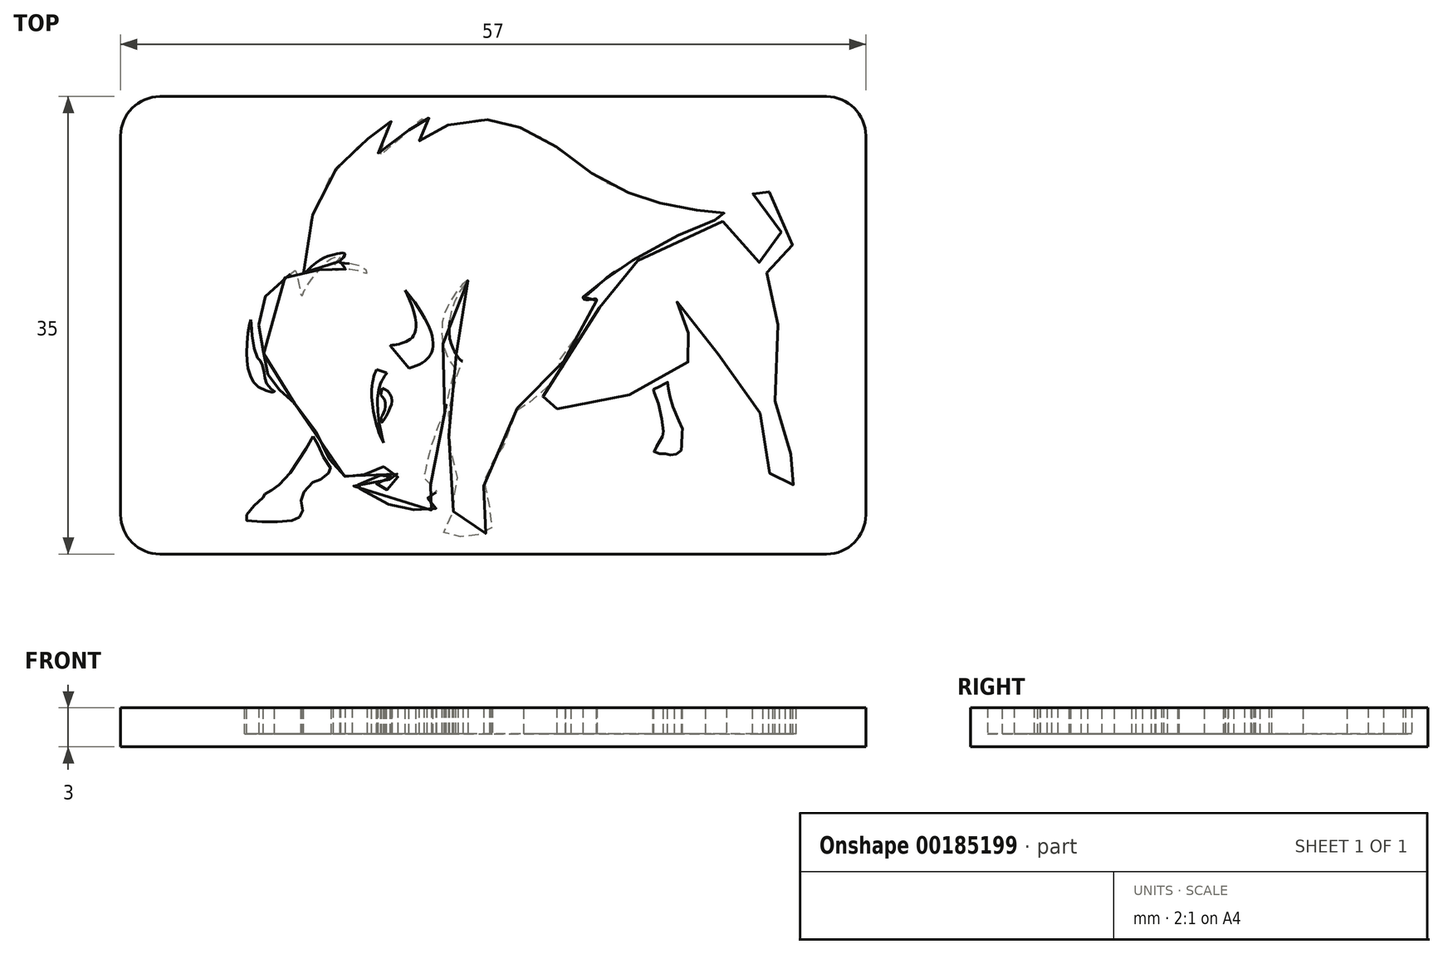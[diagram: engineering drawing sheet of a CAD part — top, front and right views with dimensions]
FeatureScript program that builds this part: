
annotation { "Feature Type Name" : "Feature", "Feature Type Description" : "" }
export const myFeature = defineFeature(function(context is Context, id is Id, definition is map)
    precondition{}
    {
        {
            var Q0;
            Q0=qCreatedBy(makeId("Top.planeOp"),FACE);
            var sketch = newSketch(context, id + "F0", { "sketchPlane" : qUnion([Q0])});
            skLineSegment(sketch, "E0.bottom", {"start": v(25.5, 17.5) * mm, "end": v(-25.5, 17.5) * mm});
            skLineSegment(sketch, "E0.top", {"start": v(25.5, -17.5) * mm, "end": v(-25.5, -17.5) * mm});
            skLineSegment(sketch, "E0.left", {"start": v(28.5, 14.5) * mm, "end": v(28.5, -14.5) * mm});
            skLineSegment(sketch, "E0.right", {"start": v(-28.5, 14.5) * mm, "end": v(-28.5, -14.5) * mm});
            skPoint(sketch, "E0.middle", {"position": v(0, 0) * mm});
            skPoint(sketch, "E1.visualSharp", {"position": v(-28.5, 17.5) * mm});
            skArc(sketch, "E1.filletArc", {"start": v(-25.5, 17.5) * mm, "mid": v(-27.62, 16.62) * mm, "end": v(-28.5, 14.5) * mm});
            skPoint(sketch, "E2.visualSharp", {"position": v(28.5, 17.5) * mm});
            skArc(sketch, "E2.filletArc", {"start": v(28.5, 14.5) * mm, "mid": v(27.62, 16.62) * mm, "end": v(25.5, 17.5) * mm});
            skPoint(sketch, "E3.visualSharp", {"position": v(28.5, -17.5) * mm});
            skArc(sketch, "E3.filletArc", {"start": v(25.5, -17.5) * mm, "mid": v(27.62, -16.62) * mm, "end": v(28.5, -14.5) * mm});
            skPoint(sketch, "E4.visualSharp", {"position": v(-28.5, -17.5) * mm});
            skArc(sketch, "E4.filletArc", {"start": v(-28.5, -14.5) * mm, "mid": v(-27.62, -16.62) * mm, "end": v(-25.5, -17.5) * mm});
            skSolve(sketch);
        }
        {
            var Q0;
            Q0=makeQuery(id+"F0.imprint","IMPRINT",FACE,{"disambiguationData":[TD([[makeQuery(id+"F0.imprint","IMPRINT",EDGE,{"derivedFrom":sQuery(id+"F0.wireOp",EDGE,"E0.bottom")}),1.0]])]});
            extrude(context, id + "F1", {"entities" : qUnion([Q0]), "depth" : 3 * mm});
        }
        {
            var Q0;
            {var subQ0=sQuery(id+"F0.wireOp",EDGE,"E4.filletArc");var subQ1=sQuery(id+"F0.wireOp",EDGE,"E3.filletArc");var subQ2=sQuery(id+"F0.wireOp",EDGE,"E2.filletArc");var subQ3=sQuery(id+"F0.wireOp",EDGE,"E1.filletArc");var subQ4=sQuery(id+"F0.wireOp",EDGE,"E0.bottom");var subQ5=sQuery(id+"F0.wireOp",EDGE,"E0.top");var subQ6=sQuery(id+"F0.wireOp",EDGE,"E0.left");var subQ7=sQuery(id+"F0.wireOp",EDGE,"E0.right");Q0=makeQuery(id+"FHE5nEUfE7JCKJp_1.boolean.opBoolean","SPLIT",FACE,{"disambiguationData":[TD([makeQuery(id+"F1.opExtrude","SWEPT_FACE",FACE,{"disambiguationData":[OSD([subQ4])]})])],"derivedFrom":makeQuery(id+"F1.opExtrude","CAP_FACE",FACE,{"disambiguationData":[OSD([subQ4,subQ5,subQ6,subQ7,subQ3,subQ2,subQ1,subQ0])],"isStart":false})});}
            var sketch = newSketch(context, id + "F2", { "sketchPlane" : qUnion([Q0])});
            skFitSpline(sketch, "E5", {"points": [v(-14.5, 4.03) * mm, v(-13.34, 9.77) * mm, v(-10.97, 13.1) * mm, v(-8.71, 14.94) * mm, v(-7.8, 15.6) * mm, v(-7.94, 15.33) * mm, v(-8.84, 12.97) * mm, v(-8.73, 12.95) * mm, v(-4.8, 16.27) * mm, v(-4.75, 16.19) * mm, v(-5.21, 15.38) * mm, v(-5.7, 14.14) * mm, v(-5.57, 14.13) * mm, v(-3.95, 15.13) * mm, v(-0.99, 15.77) * mm, v(0.92, 15.5) * mm, v(3.22, 14.63) * mm, v(6.02, 12.8) * mm, v(8.6, 10.95) * mm, v(11.2, 9.84) * mm, v(12.85, 9.32) * mm, v(15.26, 8.84) * mm, v(17.1, 8.63) * mm, v(17.75, 8.57) * mm, v(17.84, 8.52) * mm, v(17.57, 8.29) * mm, v(16.7, 7.96) * mm, v(13.8, 6.71) * mm, v(10, 4.57) * mm, v(8.54, 3.53) * mm, v(7.15, 2.34) * mm, v(6.86, 2.15) * mm, v(7, 1.99) * mm, v(7.85, 2.02) * mm, v(7.91, 1.9) * mm], "startDerivative": vector(4.07, 101.98) * mm, "endDerivative": vector(-11.12, -29.2) * mm});
            skFitSpline(sketch, "E6", {"points": [v(7.91, 1.9) * mm, v(7.4, 0.74) * mm, v(6.45, -0.72) * mm, v(5.28, -2.23) * mm, v(4.87, -2.58) * mm, v(4.96, -2.86) * mm, v(5.49, -2.73) * mm, v(5.53, -2.84) * mm, v(5.07, -3.53) * mm, v(4.15, -4.71) * mm, v(3.37, -5.44) * mm, v(2.36, -6.12) * mm, v(1.87, -6.3) * mm, v(1.82, -6.4) * mm, v(0.78, -9.2) * mm, v(0.72, -9.36) * mm, v(0.36, -9.87) * mm, v(-0.4, -11) * mm, v(-0.7, -11.93) * mm, v(-0.64, -12.94) * mm, v(-0.25, -13.77) * mm, v(-0.2, -13.92) * mm, v(-0.3, -14.08) * mm, v(-0.28, -14.2) * mm, v(-0.14, -14.67) * mm, v(-0.07, -15.15) * mm, v(-0.14, -15.55) * mm, v(-0.44, -15.86) * mm, v(-1.06, -16.02) * mm, v(-1.88, -16.11) * mm, v(-2.07, -16.16) * mm, v(-3.65, -16.17) * mm, v(-3.73, -16.12) * mm, v(-3.76, -15.74) * mm, v(-3.08, -14.32) * mm, v(-3.06, -14.23) * mm, v(-3.1, -14.12) * mm, v(-3.12, -13.53) * mm, v(-2.73, -12.2) * mm, v(-2.7, -12.02) * mm, v(-2.73, -11.59) * mm, v(-3.1, -10.3) * mm, v(-3.44, -7.36) * mm, v(-3, -4.6) * mm, v(-2.43, -2.98) * mm, v(-2.31, -2.88) * mm, v(-2.37, -2.73) * mm, v(-2.5, -2.67) * mm, v(-2.58, -2.59) * mm, v(-2.97, -1.96) * mm, v(-3.32, -1.02) * mm, v(-3.3, 0.44) * mm, v(-2.89, 1.9) * mm, v(-2.23, 3.01) * mm, v(-1.96, 3.38) * mm, v(-1.96, 3.45) * mm, v(-2.03, 3.45) * mm, v(-2.08, 3.38) * mm, v(-2.2, 3.27) * mm, v(-2.73, 2.68) * mm, v(-3.5, 1.42) * mm, v(-3.87, 0.35) * mm, v(-3.87, -1.18) * mm, v(-3.3, -2.8) * mm, v(-2.9, -3.27) * mm, v(-2.89, -3.34) * mm, v(-2.96, -3.54) * mm, v(-3.1, -3.92) * mm, v(-3.64, -6.5) * mm, v(-3.63, -6.64) * mm, v(-3.69, -6.66) * mm, v(-3.85, -6.93) * mm, v(-4.05, -7.32) * mm, v(-4.9, -9.8) * mm, v(-5.23, -11.26) * mm, v(-5.3, -11.58) * mm, v(-5.3, -11.64) * mm, v(-5.2, -11.76) * mm, v(-4.36, -12.7) * mm, v(-4.36, -12.76) * mm, v(-4.44, -12.8) * mm, v(-5.02, -12.84) * mm, v(-5.09, -12.9) * mm, v(-5.07, -13.02) * mm, v(-4.96, -13.34) * mm, v(-4.73, -13.67) * mm, v(-4.44, -13.94) * mm, v(-4.37, -13.96) * mm, v(-4.4, -14.02) * mm, v(-4.46, -14.05) * mm, v(-4.99, -14.16) * mm, v(-6.43, -14.07) * mm, v(-7.08, -14.01) * mm, v(-8.66, -13.37) * mm, v(-9.93, -12.63) * mm, v(-10.72, -12.26) * mm, v(-10.79, -12.17) * mm, v(-10.69, -12.18) * mm, v(-10.3, -12.19) * mm, v(-9.5, -11.94) * mm, v(-8.64, -11.46) * mm, v(-8.3, -11.32) * mm, v(-7.96, -11.32) * mm, v(-7.76, -11.52) * mm, v(-7.81, -11.7) * mm, v(-8.24, -11.9) * mm, v(-8.9, -12.05) * mm, v(-8.92, -12.13) * mm, v(-8.9, -12.22) * mm, v(-8.4, -12.57) * mm, v(-8.29, -12.62) * mm, v(-8.18, -12.6) * mm, v(-7.5, -12.3) * mm, v(-7.33, -12.1) * mm, v(-7.31, -11.54) * mm, v(-7.55, -11.08) * mm, v(-8.1, -10.82) * mm, v(-8.76, -10.9) * mm, v(-9.44, -11.2) * mm, v(-9.86, -11.44) * mm, v(-10.14, -11.54) * mm, v(-11.24, -11.62) * mm, v(-11.38, -11.53) * mm, v(-11.52, -11.44) * mm, v(-12.28, -10.63) * mm, v(-13.1, -9.06) * mm, v(-13.65, -8) * mm, v(-14.76, -6.58) * mm, v(-15.73, -5.18) * mm, v(-15.84, -5.1) * mm, v(-16.37, -4.9) * mm, v(-16.8, -4.55) * mm, v(-17.1, -4.19) * mm, v(-17.3, -3.27) * mm, v(-17.44, -2.65) * mm, v(-17.71, -1.46) * mm, v(-17.89, -0.55) * mm, v(-17.92, 0.78) * mm, v(-17.5, 2.1) * mm, v(-16.75, 3.05) * mm, v(-15.22, 4.15) * mm, v(-15.12, 4.2) * mm, v(-15.07, 4.1) * mm, v(-15.04, 3.94) * mm, v(-14.7, 2.3) * mm, v(-14.67, 2.23) * mm, v(-14.63, 2.25) * mm, v(-14.6, 2.38) * mm, v(-13.69, 3.8) * mm, v(-12.7, 4.92) * mm, v(-12.38, 5.13) * mm, v(-11.7, 5.32) * mm, v(-11.68, 5.28) * mm, v(-11.93, 4.96) * mm, v(-12.25, 4.32) * mm, v(-12.16, 4.17) * mm, v(-11.9, 4.26) * mm, v(-11.17, 4.3) * mm, v(-10.5, 4.25) * mm, v(-9.8, 4) * mm, v(-9.73, 3.94) * mm, v(-9.66, 4) * mm, v(-9.64, 4.1) * mm, v(-9.72, 4.24) * mm, v(-10.6, 4.67) * mm, v(-11.71, 4.8) * mm, v(-11.75, 4.85) * mm, v(-11.65, 4.98) * mm, v(-11.35, 5.34) * mm, v(-11.35, 5.48) * mm, v(-11.47, 5.53) * mm, v(-11.77, 5.5) * mm, v(-12.4, 5.36) * mm, v(-13.34, 4.94) * mm, v(-14.42, 4.02) * mm, v(-14.5, 3.99) * mm, v(-14.5, 4.03) * mm], "startDerivative": vector(-53.32, -133) * mm, "endDerivative": vector(-2.75, 33.74) * mm});
            skLineSegment(sketch, "E7", {"start": v(-8.92, -3.37) * mm, "end": v(-8.15, -3.64) * mm});
            skFitSpline(sketch, "E8", {"points": [v(-8.15, -3.64) * mm, v(-8.16, -3.7) * mm, v(-8.23, -3.78) * mm, v(-8.53, -4.26) * mm, v(-8.77, -4.95) * mm, v(-8.86, -5.67) * mm, v(-8.83, -6.53) * mm, v(-8.7, -7.64) * mm, v(-8.38, -9) * mm], "startDerivative": vector(0.8, -1.62) * mm, "endDerivative": vector(1.86, -7.3) * mm});
            skFitSpline(sketch, "E9", {"points": [v(-8.38, -9) * mm, v(-8.78, -8.12) * mm, v(-9.14, -6.74) * mm, v(-9.3, -5.37) * mm, v(-9.18, -4.1) * mm, v(-8.92, -3.37) * mm], "startDerivative": vector(-2.22, 4.49) * mm, "endDerivative": vector(1.72, 4.1) * mm});
            skFitSpline(sketch, "E10", {"points": [v(-8.48, -4.8) * mm, v(-8.28, -4.9) * mm, v(-8.03, -5.08) * mm, v(-7.81, -5.38) * mm, v(-7.76, -5.76) * mm, v(-7.8, -6.09) * mm, v(-8.01, -6.6) * mm, v(-8.3, -7.13) * mm, v(-8.5, -7.4) * mm, v(-8.53, -7.4) * mm, v(-8.54, -7.35) * mm, v(-8.57, -7.04) * mm, v(-8.54, -7) * mm, v(-8.4, -6.76) * mm, v(-8.32, -6.56) * mm, v(-8.25, -6.23) * mm, v(-8.27, -5.83) * mm, v(-8.39, -5.57) * mm, v(-8.6, -5.33) * mm, v(-8.6, -5.3) * mm, v(-8.5, -4.83) * mm, v(-8.48, -4.8) * mm]});
            skLineSegment(sketch, "E11", {"start": v(-7.84, -1.61) * mm, "end": v(-6.43, -3.29) * mm});
            skFitSpline(sketch, "E12", {"points": [v(-7.84, -1.61) * mm, v(-7.84, -1.53) * mm, v(-6.85, -1.31) * mm, v(-6.72, 2.67) * mm], "startDerivative": vector(-0.95, 3.07) * mm, "endDerivative": vector(-7.1, 15.2) * mm});
            skFitSpline(sketch, "E13", {"points": [v(-6.72, 2.67) * mm, v(-6.43, -3.29) * mm], "startDerivative": vector(9.14, -11.11) * mm, "endDerivative": vector(-6.63, -1.76) * mm});
            skFitSpline(sketch, "E14", {"points": [v(17.56, 7.97) * mm, v(14.5, 6.71) * mm, v(11.65, 5.26) * mm, v(10.45, 4.56) * mm, v(10.35, 4.45) * mm, v(9.52, 3.5) * mm, v(8.5, 1.92) * mm, v(7.34, 0.1) * mm, v(6.15, -1.64) * mm, v(5.54, -2.39) * mm, v(5.54, -2.4) * mm, v(5.7, -2.4) * mm, v(5.88, -2.44) * mm, v(5.96, -2.54) * mm, v(5.96, -2.69) * mm, v(5.81, -2.96) * mm, v(4.9, -4.28) * mm, v(3.6, -5.62) * mm, v(2.4, -6.41) * mm, v(2.36, -6.43) * mm, v(2.36, -6.47) * mm, v(2.42, -6.48) * mm, v(3.06, -6.43) * mm, v(5.39, -6.36) * mm, v(7.54, -6.1) * mm, v(8.86, -5.8) * mm, v(10.85, -5.16) * mm, v(12.66, -4.4) * mm, v(13.44, -3.85) * mm, v(14.72, -2.92) * mm, v(16.21, -2.07) * mm, v(16.26, -2.04) * mm, v(16.21, -1.97) * mm, v(15.87, -1.71) * mm, v(15.48, -1.28) * mm, v(14.94, -0.63) * mm, v(14.42, 0.34) * mm, v(13.99, 1.54) * mm, v(13.9, 2.2) * mm, v(13.9, 2.22) * mm, v(13.96, 2.22) * mm, v(13.98, 2.15) * mm, v(14.3, 1.12) * mm, v(15.4, -0.49) * mm, v(16.67, -1.85) * mm, v(17.35, -2.29) * mm, v(18.68, -3.64) * mm, v(19.48, -4.85) * mm, v(20.6, -7.13) * mm, v(21.23, -9.34) * mm, v(21.4, -10.55) * mm, v(21.37, -10.64) * mm, v(21.17, -11.24) * mm, v(21.1, -11.96) * mm, v(21.1, -11.99) * mm, v(21.29, -12.12) * mm, v(21.94, -12.33) * mm, v(22.1, -12.34) * mm, v(22.34, -12.32) * mm, v(22.79, -12.26) * mm, v(23.14, -12.11) * mm, v(23.17, -12.08) * mm, v(23.17, -11.9) * mm, v(23.1, -11.62) * mm, v(22.95, -11.18) * mm, v(22.76, -10.84) * mm, v(22.73, -10.81) * mm, v(22.77, -9.89) * mm, v(22.77, -9.85) * mm, v(22.37, -9.03) * mm, v(21.89, -7.8) * mm, v(21.61, -6.73) * mm, v(21.6, -5.27) * mm, v(21.87, -2.84) * mm, v(21.86, -1.13) * mm, v(21.62, 1.1) * mm, v(20.96, 3.19) * mm, v(20.66, 3.83) * mm, v(20.68, 3.97) * mm, v(20.79, 4.04) * mm, v(21.02, 4.02) * mm, v(21.82, 4.06) * mm, v(21.9, 4.07) * mm, v(22.41, 4.28) * mm, v(22.82, 4.8) * mm, v(22.9, 6.03) * mm, v(22.34, 7.64) * mm, v(21.44, 9.32) * mm, v(21.4, 9.44) * mm, v(21.4, 9.7) * mm, v(20.8, 10.58) * mm, v(20.4, 11.11) * mm, v(20.33, 11.33) * mm, v(20.32, 11.35) * mm, v(20.25, 11.27) * mm, v(20.04, 10.92) * mm, v(19.86, 10.37) * mm, v(19.91, 9.94) * mm, v(20.3, 9.48) * mm, v(20.77, 9.26) * mm, v(20.93, 9.14) * mm, v(21.55, 8.29) * mm, v(22.18, 6.67) * mm, v(22.35, 5.79) * mm, v(22.14, 5.08) * mm, v(21.3, 4.66) * mm, v(20.28, 4.84) * mm, v(20.2, 4.93) * mm, v(19.32, 6.25) * mm, v(18.14, 7.5) * mm, v(17.6, 7.97) * mm, v(17.56, 7.97) * mm]});
            skFitSpline(sketch, "E15", {"points": [v(13.08, -4.48) * mm, v(13.33, -4.32) * mm, v(13.34, -4.44) * mm, v(13.46, -5.13) * mm, v(13.76, -6.24) * mm, v(14.48, -7.92) * mm, v(14.5, -7.96) * mm, v(14.47, -8.14) * mm, v(14.41, -9.47) * mm, v(14.4, -9.53) * mm, v(14.1, -9.8) * mm, v(13.77, -9.9) * mm, v(13.25, -9.9) * mm, v(13.16, -9.8) * mm, v(12.62, -9.8) * mm, v(12.3, -9.66) * mm, v(12.3, -9.61) * mm, v(12.97, -8.46) * mm, v(13.03, -8.3) * mm, v(12.76, -6.45) * mm, v(12.26, -4.98) * mm, v(12.24, -4.9) * mm, v(12.3, -4.88) * mm, v(12.85, -4.62) * mm, v(13.08, -4.48) * mm]});
            skFitSpline(sketch, "E16", {"points": [v(-13.77, -8.5) * mm, v(-13.69, -8.6) * mm, v(-13.2, -9.58) * mm, v(-12.85, -10.3) * mm, v(-12.4, -10.95) * mm, v(-12.4, -11) * mm, v(-12.55, -11.23) * mm, v(-13.04, -11.72) * mm, v(-13.35, -11.81) * mm, v(-13.78, -12) * mm, v(-14.42, -12.69) * mm, v(-14.7, -13.19) * mm, v(-14.64, -13.69) * mm, v(-14.6, -14.24) * mm, v(-14.71, -14.57) * mm, v(-14.96, -14.77) * mm, v(-15.24, -14.89) * mm, v(-16.38, -15.03) * mm, v(-17.73, -15.03) * mm, v(-18.95, -14.9) * mm, v(-19.03, -14.8) * mm, v(-18.73, -14.31) * mm, v(-18.16, -13.69) * mm, v(-17.6, -13.2) * mm, v(-17.58, -13.16) * mm, v(-17.6, -13.03) * mm, v(-17.5, -12.92) * mm, v(-17.29, -12.78) * mm, v(-16.92, -12.6) * mm, v(-16.52, -12.3) * mm, v(-15.68, -11.47) * mm, v(-13.81, -8.58) * mm, v(-13.77, -8.5) * mm]});
            skFitSpline(sketch, "E17", {"points": [v(-18.55, 0.43) * mm, v(-18.59, 0.34) * mm, v(-18.8, -0.86) * mm, v(-18.86, -2.32) * mm, v(-18.77, -3.24) * mm, v(-18.47, -4.1) * mm, v(-18, -4.7) * mm, v(-17.06, -5.09) * mm, v(-16.8, -5.12) * mm, v(-16.72, -5.05) * mm, v(-16.88, -4.94) * mm, v(-17.34, -4.42) * mm, v(-17.46, -3.97) * mm, v(-17.57, -3.33) * mm, v(-17.8, -2.74) * mm, v(-17.87, -2.7) * mm, v(-18.29, -1.76) * mm, v(-18.53, 0.29) * mm, v(-18.55, 0.43) * mm]});
            skLineSegment(sketch, "E18", {"start": v(-45.55, 8.83) * mm, "end": v(-45.55, -2.67) * mm});
            skSolve(sketch);
        }
        {
            var Q0;
            Q0=qSketchRegion(id+"F2",true);
            extrude(context, id + "F3", {"entities" : qUnion([Q0]), "operationType" : NewBodyOperationType.REMOVE, "oppositeDirection" : true, "depth" : 2 * mm});
        }
    });
